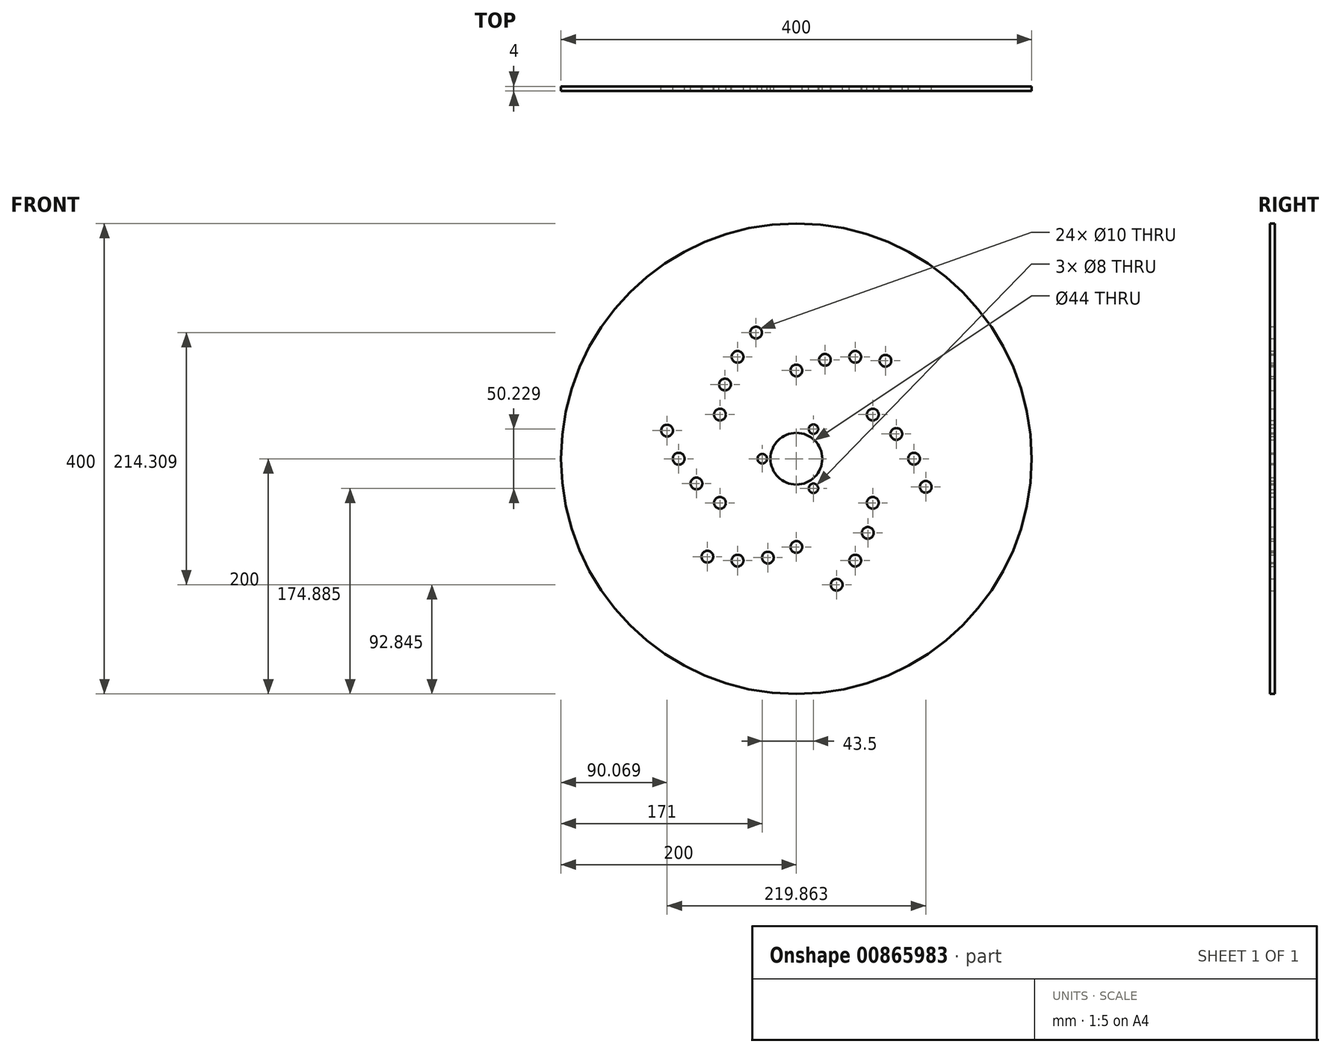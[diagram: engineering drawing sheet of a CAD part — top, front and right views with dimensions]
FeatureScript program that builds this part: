
annotation { "Feature Type Name" : "Feature", "Feature Type Description" : "" }
export const myFeature = defineFeature(function(context is Context, id is Id, definition is map)
    precondition{}
    {
        {
            var Q0;
            Q0=qCreatedBy(makeId("Front.planeOp"),FACE);
            var sketch = newSketch(context, id + "F0", { "sketchPlane" : qUnion([Q0])});
            skCircle(sketch, "E0", {"center": v(0, 0) * mm, "radius": 200 * mm});
            skCircle(sketch, "E1", {"center": v(0, 0) * mm, "radius": 22 * mm});
            skLineSegment(sketch, "E2", {"start": v(0, 0) * mm, "end": v(0, 200) * mm, "construction": true});
            skCircle(sketch, "E3", {"center": v(0, 0) * mm, "radius": 75 * mm, "construction": true});
            skCircle(sketch, "E4", {"center": v(0, 0) * mm, "radius": 87.5 * mm, "construction": true});
            skCircle(sketch, "E5", {"center": v(0, 0) * mm, "radius": 100 * mm, "construction": true});
            skCircle(sketch, "E6", {"center": v(0, 75) * mm, "radius": 5 * mm});
            skLineSegment(sketch, "E7", {"start": v(0, 0) * mm, "end": v(100, 173.2) * mm, "construction": true});
            skCircle(sketch, "E8", {"center": v(50, 86.6) * mm, "radius": 5 * mm});
            skCircle(sketch, "E9", {"center": v(24.24, 84.08) * mm, "radius": 25.88 * mm, "construction": true});
            skCircle(sketch, "E10", {"center": v(24.24, 84.08) * mm, "radius": 5 * mm});
            skCircle(sketch, "E11", {"center": v(0, 0) * mm, "radius": 29 * mm, "construction": true});
            skCircle(sketch, "E12", {"center": v(14.5, 25.11) * mm, "radius": 4 * mm});
            skCircle(sketch, "E13.1.0", {"center": v(-29, 0) * mm, "radius": 4 * mm});
            skCircle(sketch, "E13.2.0", {"center": v(14.5, -25.11) * mm, "radius": 4 * mm});
            skCircle(sketch, "E14", {"center": v(0, 0) * mm, "radius": 112.5 * mm, "construction": true});
            skCircle(sketch, "E15", {"center": v(50, 86.6) * mm, "radius": 25.88 * mm, "construction": true});
            skCircle(sketch, "E16", {"center": v(75.67, 83.25) * mm, "radius": 5 * mm});
            skCircle(sketch, "E17.1.0", {"center": v(-34.27, 107.15) * mm, "radius": 5 * mm});
            skCircle(sketch, "E17.1.1", {"center": v(-50, 86.6) * mm, "radius": 5 * mm});
            skCircle(sketch, "E17.1.2", {"center": v(-60.7, 63.03) * mm, "radius": 5 * mm});
            skCircle(sketch, "E17.1.3", {"center": v(-64.95, 37.5) * mm, "radius": 5 * mm});
            skCircle(sketch, "E17.2.0", {"center": v(-109.93, 23.9) * mm, "radius": 5 * mm});
            skCircle(sketch, "E17.2.1", {"center": v(-100, 0) * mm, "radius": 5 * mm});
            skCircle(sketch, "E17.2.2", {"center": v(-84.93, -21.04) * mm, "radius": 5 * mm});
            skCircle(sketch, "E17.2.3", {"center": v(-64.95, -37.5) * mm, "radius": 5 * mm});
            skCircle(sketch, "E18.2.3.0", {"center": v(-50, -86.6) * mm, "radius": 5 * mm});
            skCircle(sketch, "E18.4.3.0", {"center": v(-24.24, -84.08) * mm, "radius": 5 * mm});
            skCircle(sketch, "E18.6.3.0", {"center": v(0, -75) * mm, "radius": 5 * mm});
            skCircle(sketch, "E18.7.3.0", {"center": v(-75.67, -83.25) * mm, "radius": 5 * mm});
            skCircle(sketch, "E18.2.4.0", {"center": v(50, -86.6) * mm, "radius": 5 * mm});
            skCircle(sketch, "E18.4.4.0", {"center": v(60.7, -63.03) * mm, "radius": 5 * mm});
            skCircle(sketch, "E18.6.4.0", {"center": v(64.95, -37.5) * mm, "radius": 5 * mm});
            skCircle(sketch, "E18.7.4.0", {"center": v(34.27, -107.15) * mm, "radius": 5 * mm});
            skCircle(sketch, "E18.2.5.0", {"center": v(100, 0) * mm, "radius": 5 * mm});
            skCircle(sketch, "E18.4.5.0", {"center": v(84.93, 21.04) * mm, "radius": 5 * mm});
            skCircle(sketch, "E18.6.5.0", {"center": v(64.95, 37.5) * mm, "radius": 5 * mm});
            skCircle(sketch, "E18.7.5.0", {"center": v(109.93, -23.9) * mm, "radius": 5 * mm});
            skSolve(sketch);
        }
        {
            var Q0;
            Q0=makeQuery(id+"F0.imprint","IMPRINT",FACE,{"disambiguationData":[TD([[makeQuery(id+"F0.imprint","IMPRINT",EDGE,{"derivedFrom":sQuery(id+"F0.wireOp",EDGE,"E0")}),1.0]])]});
            extrude(context, id + "F1", {"entities" : qUnion([Q0]), "depth" : 4 * mm, "offsetDistance" : 25 * mm});
        }
    });
